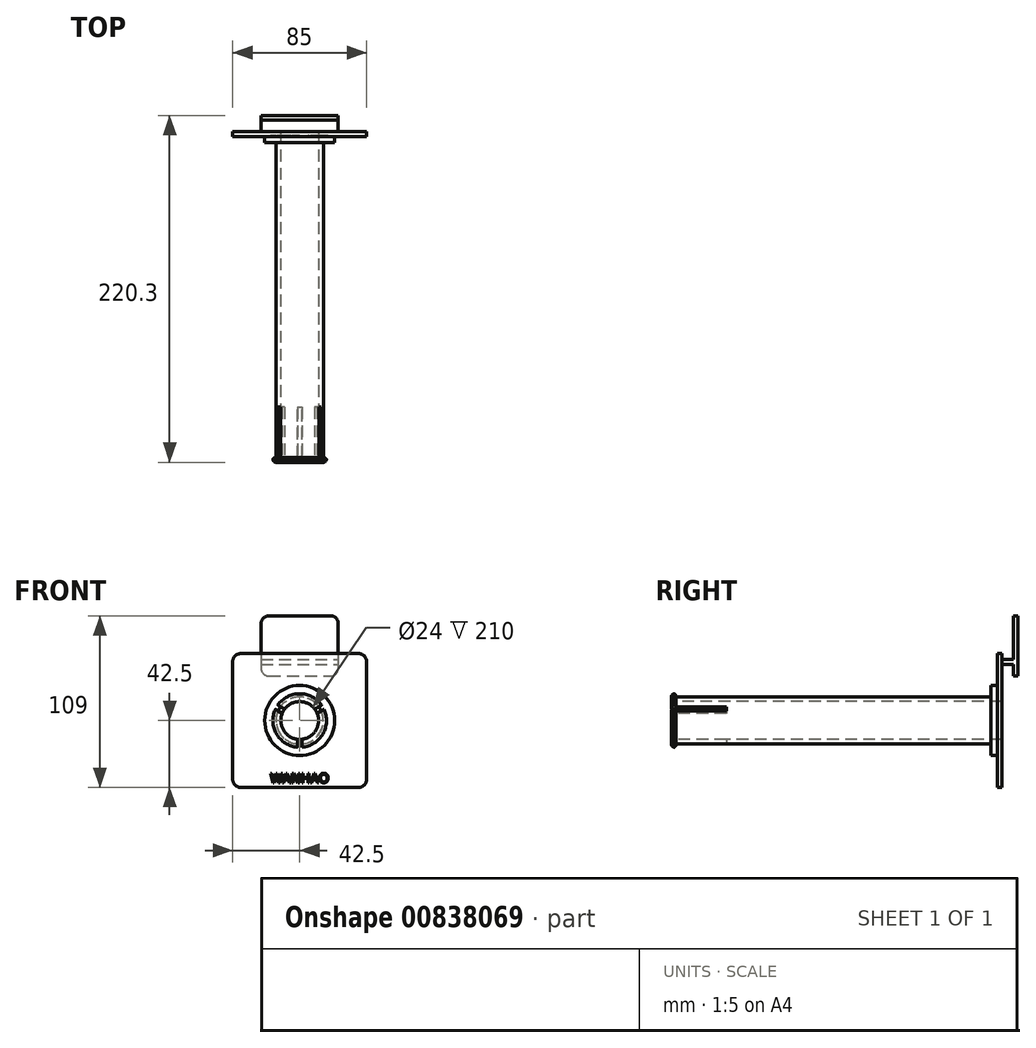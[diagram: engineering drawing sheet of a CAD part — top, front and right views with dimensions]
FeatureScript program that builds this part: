
annotation { "Feature Type Name" : "Feature", "Feature Type Description" : "" }
export const myFeature = defineFeature(function(context is Context, id is Id, definition is map)
    precondition{}
    {
        {
            assignVariable(context, id + "F0", {"name" : "BaseRingHeight", "anyValue" : 4});
        }
        {
            assignVariable(context, id + "F1", {"name" : "SpoolRingHeight", "anyValue" : 200});
        }
        {
            var Q0;
            Q0=qCreatedBy(makeId("Front.planeOp"),FACE);
            var sketch = newSketch(context, id + "F2", { "sketchPlane" : qUnion([Q0])});
            skLineSegment(sketch, "E0.bottom", {"start": v(-44, 38.3) * mm, "end": v(-5, 38.3) * mm});
            skLineSegment(sketch, "E0.top", {"start": v(-44, 0) * mm, "end": v(-5, 0) * mm});
            skLineSegment(sketch, "E0.left", {"start": v(-49, 33.3) * mm, "end": v(-49, 5) * mm});
            skLineSegment(sketch, "E0.right", {"start": v(0, 33.3) * mm, "end": v(0, 5) * mm});
            skPoint(sketch, "E1.visualSharp", {"position": v(-49, 38.3) * mm});
            skArc(sketch, "E1.filletArc", {"start": v(-44, 38.3) * mm, "mid": v(-47.54, 36.84) * mm, "end": v(-49, 33.3) * mm});
            skPoint(sketch, "E2.visualSharp", {"position": v(0, 38.3) * mm});
            skArc(sketch, "E2.filletArc", {"start": v(0, 33.3) * mm, "mid": v(-1.46, 36.84) * mm, "end": v(-5, 38.3) * mm});
            skPoint(sketch, "E3.visualSharp", {"position": v(0, 0) * mm});
            skArc(sketch, "E3.filletArc", {"start": v(-5, 0) * mm, "mid": v(-1.46, 1.46) * mm, "end": v(0, 5) * mm});
            skPoint(sketch, "E4.visualSharp", {"position": v(-49, 0) * mm});
            skArc(sketch, "E4.filletArc", {"start": v(-49, 5) * mm, "mid": v(-47.54, 1.46) * mm, "end": v(-44, 0) * mm});
            skSolve(sketch);
        }
        {
            var Q0;
            Q0 = qSketchRegion(id + "F2", true);
            extrude(context, id + "F3", {"entities" : qUnion([Q0]), "depth" : 3 * mm, "offsetDistance" : 25 * mm});
        }
        {
            var Q0;
            Q0=makeQuery(id+"F3.opExtrude","CAP_FACE",FACE,{"disambiguationData":[OSD([sQuery(id+"F2.wireOp",EDGE,"E0.bottom"),sQuery(id+"F2.wireOp",EDGE,"E0.top"),sQuery(id+"F2.wireOp",EDGE,"E0.left"),sQuery(id+"F2.wireOp",EDGE,"E0.right")])],"isStart":false});
            var sketch = newSketch(context, id + "F4", { "sketchPlane" : qUnion([Q0])});
            skLineSegment(sketch, "E5.bottom", {"start": v(-49, 10.5) * mm, "end": v(0, 10.5) * mm});
            skLineSegment(sketch, "E5.top", {"start": v(-49, 7.5) * mm, "end": v(0, 7.5) * mm});
            skLineSegment(sketch, "E5.left", {"start": v(-49, 10.5) * mm, "end": v(-49, 7.5) * mm});
            skLineSegment(sketch, "E5.right", {"start": v(0, 10.5) * mm, "end": v(0, 7.5) * mm});
            skSolve(sketch);
        }
        {
            var Q0;
            Q0 = qSketchRegion(id + "F4", true);
            extrude(context, id + "F5", {"entities" : qUnion([Q0]), "operationType" : NewBodyOperationType.ADD, "depth" : 7.3 * mm, "offsetDistance" : 25 * mm});
        }
        {
            var Q0;
            Q0=makeQuery(id+"F5.opExtrude","CAP_FACE",FACE,{"disambiguationData":[OSD([sQuery(id+"F4.wireOp",EDGE,"E5.bottom"),sQuery(id+"F4.wireOp",EDGE,"E5.top"),sQuery(id+"F4.wireOp",EDGE,"E5.left"),sQuery(id+"F4.wireOp",EDGE,"E5.right")])],"isStart":false});
            var sketch = newSketch(context, id + "F6", { "sketchPlane" : qUnion([Q0])});
            skLineSegment(sketch, "E6.bottom", {"start": v(-62, 14.3) * mm, "end": v(13, 14.3) * mm});
            skLineSegment(sketch, "E6.top", {"start": v(-62, -70.7) * mm, "end": v(13, -70.7) * mm});
            skLineSegment(sketch, "E6.left", {"start": v(-67, 9.3) * mm, "end": v(-67, -65.7) * mm});
            skLineSegment(sketch, "E6.right", {"start": v(18, 9.3) * mm, "end": v(18, -65.7) * mm});
            skPoint(sketch, "E7.visualSharp", {"position": v(-67, 14.3) * mm});
            skArc(sketch, "E7.filletArc", {"start": v(-62, 14.3) * mm, "mid": v(-65.54, 12.84) * mm, "end": v(-67, 9.3) * mm});
            skPoint(sketch, "E8.visualSharp", {"position": v(18, 14.3) * mm});
            skArc(sketch, "E8.filletArc", {"start": v(18, 9.3) * mm, "mid": v(16.54, 12.84) * mm, "end": v(13, 14.3) * mm});
            skPoint(sketch, "E9.visualSharp", {"position": v(18, -70.7) * mm});
            skArc(sketch, "E9.filletArc", {"start": v(13, -70.7) * mm, "mid": v(16.54, -69.24) * mm, "end": v(18, -65.7) * mm});
            skPoint(sketch, "E10.visualSharp", {"position": v(-67, -70.7) * mm});
            skArc(sketch, "E10.filletArc", {"start": v(-67, -65.7) * mm, "mid": v(-65.54, -69.24) * mm, "end": v(-62, -70.7) * mm});
            skSolve(sketch);
        }
        {
            var Q0;
            Q0 = qSketchRegion(id + "F6", true);
            extrude(context, id + "F7", {"entities" : qUnion([Q0]), "operationType" : NewBodyOperationType.ADD, "depth" : 3 * mm, "offsetDistance" : 25 * mm});
        }
        {
            var Q0;
            Q0=makeQuery(id+"F7.opExtrude","CAP_FACE",FACE,{"disambiguationData":[OSD([sQuery(id+"F6.wireOp",EDGE,"E6.bottom"),sQuery(id+"F6.wireOp",EDGE,"E6.top"),sQuery(id+"F6.wireOp",EDGE,"E6.left"),sQuery(id+"F6.wireOp",EDGE,"E6.right"),sQuery(id+"F6.wireOp",EDGE,"E7.filletArc"),sQuery(id+"F6.wireOp",EDGE,"E8.filletArc"),sQuery(id+"F6.wireOp",EDGE,"E9.filletArc"),sQuery(id+"F6.wireOp",EDGE,"E10.filletArc")])],"isStart":false});
            var sketch = newSketch(context, id + "F8", { "sketchPlane" : qUnion([Q0])});
            skCircle(sketch, "E11", {"center": v(-24.5, -28.2) * mm, "radius": 22.25 * mm});
            skLineSegment(sketch, "E12", {"start": v(-82.43, -28.2) * mm, "end": v(118.43, -28.2) * mm, "construction": true});
            skLineSegment(sketch, "E13", {"start": v(-24.5, 43.68) * mm, "end": v(-24.5, -185.08) * mm, "construction": true});
            skSolve(sketch);
        }
        {
            var Q0;
            Q0 = qSketchRegion(id + "F8", true);
            extrude(context, id + "F9", {"entities" : qUnion([Q0]), "operationType" : NewBodyOperationType.ADD, "depth" : (getVariable(context, 'BaseRingHeight')) * mm, "offsetDistance" : 25 * mm});
        }
        {
            var Q0;
            Q0=makeQuery(id+"F9.opExtrude","CAP_FACE",FACE,{"disambiguationData":[OSD([sQuery(id+"F8.wireOp",EDGE,"E11")])],"isStart":false});
            var sketch = newSketch(context, id + "F10", { "sketchPlane" : qUnion([Q0])});
            skCircle(sketch, "E14", {"center": v(-24.5, -28.2) * mm, "radius": 15 * mm});
            skSolve(sketch);
        }
        {
            var Q0;
            Q0 = qSketchRegion(id + "F10", true);
            var Q1;
            Q1 = qSketchRegion(id + "F12", true);
            extrude(context, id + "F11", {"entities" : qUnion([Q0, Q1]), "operationType" : NewBodyOperationType.ADD, "depth" : (getVariable(context, 'SpoolRingHeight')) * mm, "offsetDistance" : 25 * mm});
        }
        {
            var Q0;
            Q0=makeQuery(id+"F11.opExtrude","CAP_FACE",FACE,{"disambiguationData":[OSD([sQuery(id+"F10.wireOp",EDGE,"E14")])],"isStart":false});
            var sketch = newSketch(context, id + "F12", { "sketchPlane" : qUnion([Q0])});
            skCircle(sketch, "E15", {"center": v(-24.5, -28.2) * mm, "radius": 12 * mm});
            skSolve(sketch);
        }
        {
            var Q0;
            Q0 = qSketchRegion(id + "F12", true);
            var Q1;
            Q1=makeQuery(id+"F7.opExtrude","CAP_FACE",FACE,{"disambiguationData":[OSD([sQuery(id+"F6.wireOp",EDGE,"E6.bottom"),sQuery(id+"F6.wireOp",EDGE,"E6.top"),sQuery(id+"F6.wireOp",EDGE,"E6.left"),sQuery(id+"F6.wireOp",EDGE,"E6.right"),sQuery(id+"F6.wireOp",EDGE,"E7.filletArc"),sQuery(id+"F6.wireOp",EDGE,"E8.filletArc"),sQuery(id+"F6.wireOp",EDGE,"E9.filletArc"),sQuery(id+"F6.wireOp",EDGE,"E10.filletArc")])],"isStart":true});
            extrude(context, id + "F13", {"entities" : qUnion([Q0]), "operationType" : NewBodyOperationType.REMOVE, "endBound" : BoundingType.UP_TO_SURFACE, "oppositeDirection" : true, "depth" : 25 * mm, "endBoundEntityFace" : qUnion([Q1]), "offsetDistance" : 25 * mm});
        }
        {
            var Q0;
            {var subQ0=sQuery(id+"F10.wireOp",EDGE,"E14");Q0=makeQuery(id+"F17.boolean.opBoolean","SPLIT",FACE,{"disambiguationData":[TD([makeQuery(id+"F17.opExtrude","SWEPT_FACE",FACE,{"disambiguationData":[OSD([sQuery(id+"F16.wireOp",EDGE,"E21.left")])]})])],"derivedFrom":makeQuery(id+"F11.opExtrude","CAP_FACE",FACE,{"disambiguationData":[OSD([subQ0])],"isStart":false})});}
            var sketch = newSketch(context, id + "F14", { "sketchPlane" : qUnion([Q0])});
            skCircle(sketch, "E16", {"center": v(-24.5, -28.2) * mm, "radius": 12 * mm});
            skCircle(sketch, "E17", {"center": v(-24.5, -28.2) * mm, "radius": 17 * mm});
            skSolve(sketch);
        }
        {
            var Q0;
            Q0 = qSketchRegion(id + "F14", true);
            extrude(context, id + "F15", {"entities" : qUnion([Q0]), "operationType" : NewBodyOperationType.ADD, "depth" : 3 * mm, "offsetDistance" : 25 * mm});
        }
        {
            var Q0;
            Q0=makeQuery(id+"F15.opExtrude","CAP_FACE",FACE,{"disambiguationData":[OSD([sQuery(id+"F14.wireOp",EDGE,"E16"),sQuery(id+"F14.wireOp",EDGE,"E17")])],"isStart":false});
            var sketch = newSketch(context, id + "F16", { "sketchPlane" : qUnion([Q0])});
            skLineSegment(sketch, "E18", {"start": v(-24.5, -28.2) * mm, "end": v(-51, -12.9) * mm, "construction": true});
            skLineSegment(sketch, "E19", {"start": v(-24.5, -28.2) * mm, "end": v(2, -12.9) * mm, "construction": true});
            skLineSegment(sketch, "E20", {"start": v(-24.5, -28.2) * mm, "end": v(-24.5, -58.8) * mm, "construction": true});
            skLineSegment(sketch, "E21.bottom", {"start": v(-26, -28.2) * mm, "end": v(-23, -28.2) * mm});
            skLineSegment(sketch, "E21.top", {"start": v(-26, -58.76) * mm, "end": v(-23, -58.76) * mm});
            skLineSegment(sketch, "E21.left", {"start": v(-26, -28.2) * mm, "end": v(-26, -58.76) * mm});
            skLineSegment(sketch, "E21.right", {"start": v(-23, -28.2) * mm, "end": v(-23, -58.76) * mm});
            skCircle(sketch, "E22", {"center": v(-24.5, -28.2) * mm, "radius": 30.6 * mm, "construction": true});
            skLineSegment(sketch, "E23", {"start": v(1.22, -11.62) * mm, "end": v(2.72, -14.22) * mm});
            skLineSegment(sketch, "E24", {"start": v(2.72, -14.22) * mm, "end": v(-23.75, -29.5) * mm});
            skLineSegment(sketch, "E25", {"start": v(-23.75, -29.5) * mm, "end": v(-25.25, -26.9) * mm});
            skLineSegment(sketch, "E26", {"start": v(-25.25, -26.9) * mm, "end": v(1.22, -11.62) * mm});
            skLineSegment(sketch, "E27", {"start": v(-50.22, -11.62) * mm, "end": v(-51.72, -14.22) * mm});
            skLineSegment(sketch, "E28", {"start": v(-51.72, -14.22) * mm, "end": v(-25.25, -29.5) * mm});
            skLineSegment(sketch, "E29", {"start": v(-25.25, -29.5) * mm, "end": v(-23.75, -26.9) * mm});
            skLineSegment(sketch, "E30", {"start": v(-23.75, -26.9) * mm, "end": v(-50.22, -11.62) * mm});
            skSolve(sketch);
        }
        {
            var Q0;
            Q0 = qSketchRegion(id + "F16", true);
            extrude(context, id + "F17", {"entities" : qUnion([Q0]), "operationType" : NewBodyOperationType.REMOVE, "oppositeDirection" : true, "depth" : 70 * mm, "offsetDistance" : 25 * mm, "symmetric" : true});
        }
        {
            var Q0;
            {var subQ0=sQuery(id+"F14.wireOp",EDGE,"E17");Q0=makeQuery(id+"F17.boolean.opBoolean","SPLIT",EDGE,{"disambiguationData":[TD([makeQuery(id+"F17.opExtrude","SWEPT_FACE",FACE,{"disambiguationData":[OSD([sQuery(id+"F16.wireOp",EDGE,"E21.left")])]})])],"derivedFrom":makeQuery(id+"F15.opExtrude","CAP_EDGE",EDGE,{"disambiguationData":[OSD([subQ0])],"isStart":false})});}
            var Q1;
            {var subQ0=sQuery(id+"F14.wireOp",EDGE,"E17");Q1=makeQuery(id+"F17.boolean.opBoolean","SPLIT",EDGE,{"disambiguationData":[TD([makeQuery(id+"F17.opExtrude","SWEPT_FACE",FACE,{"disambiguationData":[OSD([sQuery(id+"F16.wireOp",EDGE,"E26")])]})])],"derivedFrom":makeQuery(id+"F15.opExtrude","CAP_EDGE",EDGE,{"disambiguationData":[OSD([subQ0])],"isStart":false})});}
            var Q2;
            {var subQ0=sQuery(id+"F14.wireOp",EDGE,"E17");Q2=makeQuery(id+"F17.boolean.opBoolean","SPLIT",EDGE,{"disambiguationData":[TD([makeQuery(id+"F17.opExtrude","SWEPT_FACE",FACE,{"disambiguationData":[OSD([sQuery(id+"F16.wireOp",EDGE,"E21.right")])]})])],"derivedFrom":makeQuery(id+"F15.opExtrude","CAP_EDGE",EDGE,{"disambiguationData":[OSD([subQ0])],"isStart":false})});}
            fillet(context, id + "F18", {"entities" : qUnion([Q0, Q1, Q2]), "radius" : 2 * mm, "tangentPropagation" : true, "allowEdgeOverflow" : false});
        }
        {
            var Q0;
            {var subQ0=sQuery(id+"F14.wireOp",EDGE,"E17");Q0=makeQuery(id+"F17.boolean.opBoolean","SPLIT",EDGE,{"disambiguationData":[TD([makeQuery(id+"F17.opExtrude","SWEPT_FACE",FACE,{"disambiguationData":[OSD([sQuery(id+"F16.wireOp",EDGE,"E21.right")])]})])],"derivedFrom":makeQuery(id+"F15.opExtrude","CAP_EDGE",EDGE,{"disambiguationData":[OSD([subQ0])],"isStart":true})});}
            var Q1;
            {var subQ0=sQuery(id+"F14.wireOp",EDGE,"E17");Q1=makeQuery(id+"F17.boolean.opBoolean","SPLIT",EDGE,{"disambiguationData":[TD([makeQuery(id+"F17.opExtrude","SWEPT_FACE",FACE,{"disambiguationData":[OSD([sQuery(id+"F16.wireOp",EDGE,"E26")])]})])],"derivedFrom":makeQuery(id+"F15.opExtrude","CAP_EDGE",EDGE,{"disambiguationData":[OSD([subQ0])],"isStart":true})});}
            var Q2;
            {var subQ0=sQuery(id+"F14.wireOp",EDGE,"E17");Q2=makeQuery(id+"F17.boolean.opBoolean","SPLIT",EDGE,{"disambiguationData":[TD([makeQuery(id+"F17.opExtrude","SWEPT_FACE",FACE,{"disambiguationData":[OSD([sQuery(id+"F16.wireOp",EDGE,"E21.left")])]})])],"derivedFrom":makeQuery(id+"F15.opExtrude","CAP_EDGE",EDGE,{"disambiguationData":[OSD([subQ0])],"isStart":true})});}
            fillet(context, id + "F19", {"entities" : qUnion([Q0, Q1, Q2]), "radius" : 2 * mm, "tangentPropagation" : true, "allowEdgeOverflow" : false});
        }
        {
            var Q0;
            Q0=makeQuery(id+"F8.imprint","IMPRINT",FACE,{"disambiguationData":[TD([[makeQuery(id+"F8.imprint","IMPRINT",EDGE,{"derivedFrom":sQuery(id+"F8.wireOp",EDGE,"E11")}),-1.0]])]});
            var sketch = newSketch(context, id + "F20", { "sketchPlane" : qUnion([Q0])});
            skText(sketch, "E31", { "text": "WANHAO", "fontName": "OpenSans-Regular.ttf"});
            skLineSegment(sketch, "E32", {"start": v(14.01, -67.7) * mm, "end": v(-56.31, -67.7) * mm, "construction": true});
            const initialGuessF20  = {"E31": [-0.0431, -0.0677, 1, 0, 0.006]};
            skSetInitialGuess(sketch, initialGuessF20);
            skSolve(sketch);
        }
        {
            var Q0;
            Q0 = qSketchRegion(id + "F20", true);
            extrude(context, id + "F21", {"entities" : qUnion([Q0]), "operationType" : NewBodyOperationType.REMOVE, "oppositeDirection" : true, "depth" : .5 * mm, "offsetDistance" : 25 * mm});
        }
    });
